# Revit family: FP-Revit20-en-ASKS60W5-ASKS60G5-StackingKit-0-90006108A-AU-NZ
name_source: partatom
category: Specialty Equipment
units: mm (PartAtom-declared; Revit-internal decimal feet)

## family parameters
Always vertical = Yes
Cut with Voids When Loaded = Yes
OmniClass Number = 23.45.70.11.11
OmniClass Title = Residential Laundry Equipment
Part Type = Normal
Room Calculation Point = No
Round Connector Dimension = Use Diameter
Shared = Yes
Work Plane-Based = No

## types (2) — shared parameters
Bracket - Offset (487,533,555,601) = 601 mm
Cavity - Depth = 688 mm
Cavity - Height = 50 mm  [stored 0.164042 ft]
Cavity - Width = 622 mm  [stored 2.04068 ft]
Chassis - Depth = 576 mm
Chassis - Height = 29 mm  [stored 0.0951444 ft]
Chassis - Width = 595 mm  [stored 1.9521 ft]
Manufacturer = Fisher & Paykel Appliances Ltd
Material - Body = Fisher & Paykel - Grey
Product - Depth = 625 mm
Product - Height = 50 mm  [stored 0.164042 ft]
Product - Width = 595 mm  [stored 1.9521 ft]
Visibility - Clearance Required = Yes
zero-valued in all types: Default Elevation

## per-type parameters (varying)
| type | Description | Material - Front |
| ASKS60G5 | Stacking Kit with Tray - Graphite | Fisher & Paykel - Graphite |
| ASKS60W5 | Stacking Kit with Tray - White | Fisher & Paykel - White |

note: column(s) folded — value = type name in every type: Model

note: [stored X ft] marks values corroborated as IEEE doubles in the binary element streams (Revit-internal decimal feet)

## geometry (parser evidence)
native form markers: Sweep x5
no freeform markers — native parametric forms only
